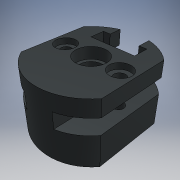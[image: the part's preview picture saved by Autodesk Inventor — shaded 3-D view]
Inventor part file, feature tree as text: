
AUTODESK INVENTOR PART (.ipt)
format: ipt  version: 2018 (Build 220112000, 112)  size: 249,856 bytes
history: native  units: mm
features: extrude x8, sketch x8, other x2
ambient origin geometry x8: Origin, YZ Plane, XZ Plane, XY Plane, X Axis, Y Axis, Z Axis, Center Point
bodies: Body1 (feature_tree)
feature tree (18):
  other  "Těleso1"
  extrude  "Vysunutí1"  Depth=28.0mm
  other  "Pracovní rovina1"
  extrude  "Vysunutí2"  Depth=20.0mm TaperAngle=0.0deg
  extrude  "Vysunutí6"  Depth=20.0mm TaperAngle=0.0deg
  extrude  "Vysunutí8"  Depth=20.0mm TaperAngle=0.0deg
  extrude  "Vysunutí9"  Depth=3.5mm
  extrude  "Vysunutí10"  Depth=3.0mm
  extrude  "Vysunutí11"  Depth=4.0mm TaperAngle=0.0deg
  extrude  "Vysunutí13"  TaperAngle=0.0deg  [1 undecoded]
  sketch  "Náčrt1"
  sketch  "Náčrt2"
  sketch  "Náčrt6"
  sketch  "Náčrt8"
  sketch  "Náčrt9"
  sketch  "Náčrt10"
  sketch  "Náčrt11"
  sketch  "Náčrt12"
note: 1 required parameter value undecoded (feature->parameter linkage not recoverable at this tier; creation-order binding heuristic only, values carry confidence <= 0.55)
